# Revit family: P400217-109
name_source: partatom
category: Lighting Fixtures
revit_build: Autodesk Revit 2014 (Build: 20130308_1515(x64)
units: mm (PartAtom-declared; Revit-internal decimal feet)

## types (1)
- P400217-109
    Apparent Load = 60 VA
    Assembly Code = D5020200
    Default Elevation = 48 "
    Description = Execute bold visions and design statements with the Rae Collection’s Nine
Light Chandelier. A blend of geometric shapes and a sculpted hand artisan
frame allows this light fixture to double as a stunning work of art. A glowing golden finish brings this modern chandelier to life for an awe-inspiring
lighting experience guaranteed to spark conversation amongst your gazing
guests.
    Features = • Sculpted hand artisan frame.
• Glowing golden brushed bronze finish.
• Geometric white alabaster shades.
• Ideal for any dining room, kitchen, or foyer.
• Perfect for luxe, mid-century modern, and modern style settings.
• 1-Year Limited Warranty
• For optimal illumination, use nine candelabra base bulbs (60w max - LED or incandescent)
• Fully dimmable with dimmable bulbs
• Able to be fully dimmable with dimmable bulbs.
• Includes installation instructions and mounting hardware.
• Progress Lighting products are designed for exceptional quality, reliability, and functionality.
    Fixture distribution = Direct
    Glass = Paint - Hubbell - White Texture
    Gold = Hubbell - Gold
    Height = 26.5 "
    Housing Material = Hubbell - Gold
    Lamp = LED or Medium Base
    Load Classification = Lighting
    Manufacturer = Progress Lighting
    Model = P400217-109
    Power Factor = 1
    Product Documentation Link = https://hubbellcdn.com
    Product Link = https://www.hubbell.com
    Steel = Paint - Hubbell - Matte White
    URL = https://www.hubbell.com
    Voltage = 120 V
    Warranty = 1 year Warranty
    Wattage Comments = 60W
    Watts = 60 W
    Width = 6 "

## geometry (parser evidence)
native form markers: Sweep x2
no freeform markers — native parametric forms only
